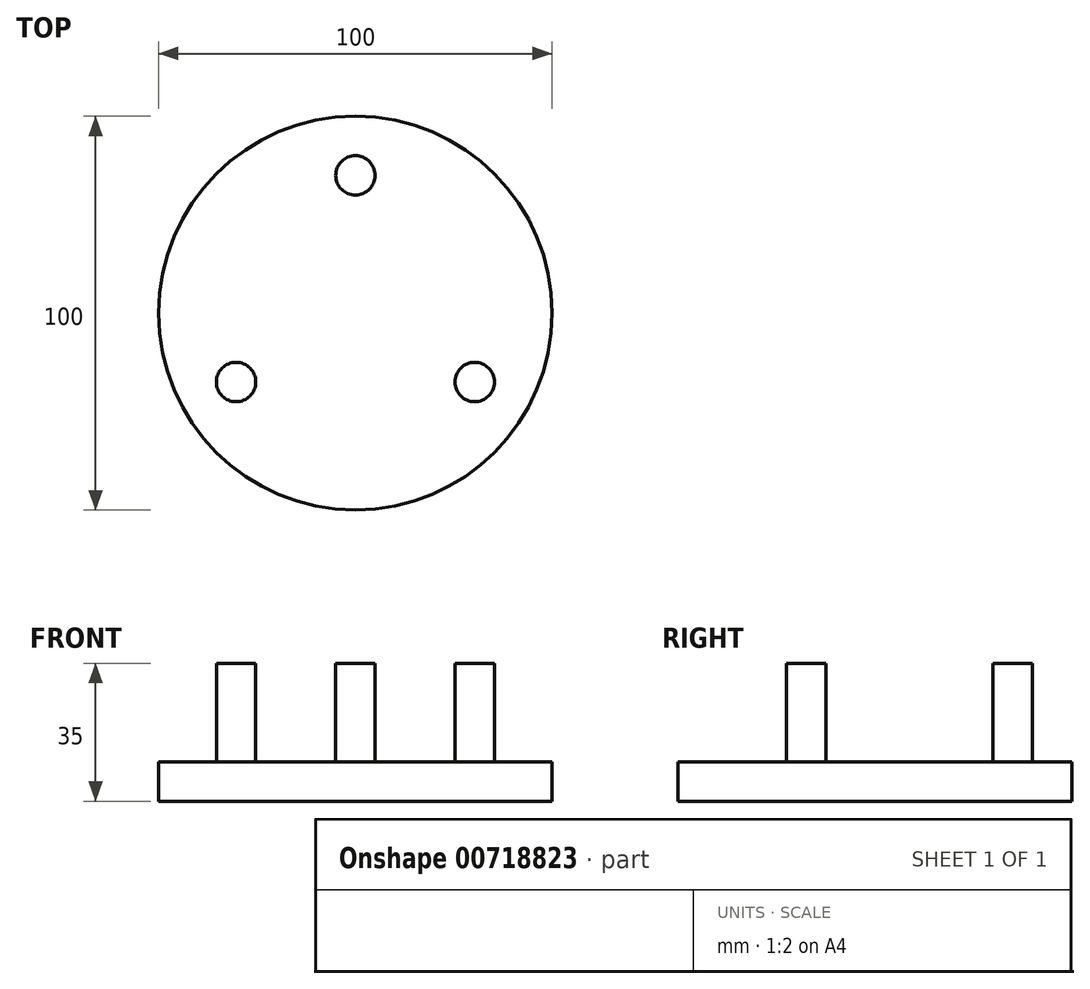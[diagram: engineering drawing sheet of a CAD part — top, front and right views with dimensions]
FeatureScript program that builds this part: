
annotation { "Feature Type Name" : "Feature", "Feature Type Description" : "" }
export const myFeature = defineFeature(function(context is Context, id is Id, definition is map)
    precondition{}
    {
        {
            var Q0;
            Q0=qCreatedBy(makeId("Top.planeOp"),FACE);
            var sketch = newSketch(context, id + "F0", { "sketchPlane" : qUnion([Q0])});
            skCircle(sketch, "E0", {"center": v(0, 0) * mm, "radius": 50 * mm});
            skSolve(sketch);
        }
        {
            var Q0;
            Q0 = qSketchRegion(id + "F0", true);
            extrude(context, id + "F1", {"entities" : qUnion([Q0]), "endBound" : BoundingType.SYMMETRIC, "depth" : 10 * mm, "offsetDistance" : 25 * mm});
        }
        {
            var Q0;
            Q0=makeQuery(id+"F1.opExtrude","CAP_FACE",FACE,{"disambiguationData":[OSD([sQuery(id+"F0.wireOp",EDGE,"E0")])],"isStart":false});
            var sketch = newSketch(context, id + "F2", { "sketchPlane" : qUnion([Q0])});
            skCircle(sketch, "E1", {"center": v(0, 35) * mm, "radius": 5 * mm});
            skCircle(sketch, "E2.1.0", {"center": v(30.31, -17.5) * mm, "radius": 5 * mm});
            skCircle(sketch, "E2.2.0", {"center": v(-30.31, -17.5) * mm, "radius": 5 * mm});
            skPoint(sketch, "E2.center", {"position": v(0, 0) * mm});
            skLineSegment(sketch, "E2.anchor1", {"start": v(0, 0) * mm, "end": v(0, 35) * mm, "construction": true});
            skLineSegment(sketch, "E2.anchor2", {"start": v(0, 0) * mm, "end": v(-30.31, -17.5) * mm, "construction": true});
            skSolve(sketch);
        }
        {
            var Q0;
            Q0 = qSketchRegion(id + "F2", true);
            extrude(context, id + "F3", {"entities" : qUnion([Q0]), "operationType" : NewBodyOperationType.ADD, "depth" : 25 * mm, "offsetDistance" : 25 * mm});
        }
    });
